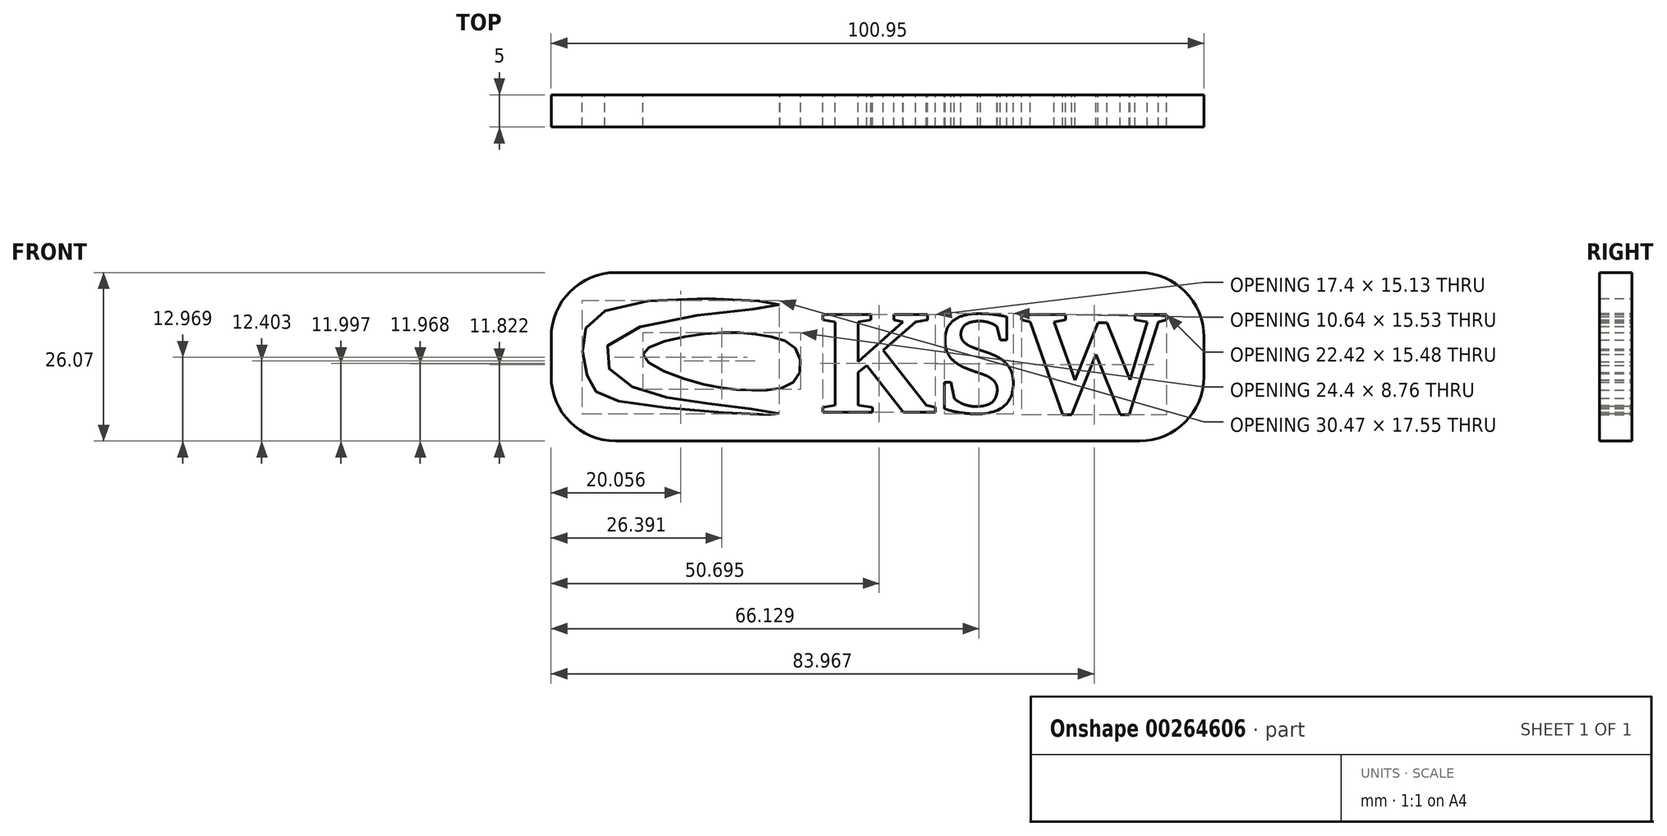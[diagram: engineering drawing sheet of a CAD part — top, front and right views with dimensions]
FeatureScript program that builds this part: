
annotation { "Feature Type Name" : "Feature", "Feature Type Description" : "" }
export const myFeature = defineFeature(function(context is Context, id is Id, definition is map)
    precondition{}
    {
        {
            var Q0;
            Q0=qCreatedBy(makeId("Front.planeOp"),FACE);
            var sketch = newSketch(context, id + "F0", { "sketchPlane" : qUnion([Q0])});
            skLineSegment(sketch, "E0.bottom", {"start": v(28.98, -26.09) * mm, "end": v(-51.97, -26.09) * mm});
            skLineSegment(sketch, "E0.top", {"start": v(28.98, -0.02) * mm, "end": v(-51.97, -0.02) * mm});
            skLineSegment(sketch, "E0.left", {"start": v(38.98, -16.09) * mm, "end": v(38.98, -10.02) * mm});
            skLineSegment(sketch, "E0.right", {"start": v(-61.97, -16.09) * mm, "end": v(-61.97, -10.02) * mm});
            skPoint(sketch, "E1.visualSharp", {"position": v(-61.97, -0.02) * mm});
            skArc(sketch, "E1.filletArc", {"start": v(-51.97, -0.02) * mm, "mid": v(-59.04, -2.95) * mm, "end": v(-61.97, -10.02) * mm});
            skPoint(sketch, "E2.visualSharp", {"position": v(-61.97, -26.09) * mm});
            skArc(sketch, "E2.filletArc", {"start": v(-61.97, -16.09) * mm, "mid": v(-59.04, -23.16) * mm, "end": v(-51.97, -26.09) * mm});
            skPoint(sketch, "E3.visualSharp", {"position": v(38.98, -26.09) * mm});
            skArc(sketch, "E3.filletArc", {"start": v(28.98, -26.09) * mm, "mid": v(36.05, -23.16) * mm, "end": v(38.98, -16.09) * mm});
            skPoint(sketch, "E4.visualSharp", {"position": v(38.98, -0.02) * mm});
            skArc(sketch, "E4.filletArc", {"start": v(38.98, -10.02) * mm, "mid": v(36.05, -2.95) * mm, "end": v(28.98, -0.02) * mm});
            skText(sketch, "E5", { "text": "KSW", "fontName": "Tinos-Bold.ttf"});
            skFitSpline(sketch, "E6", {"points": [v(-26.68, -5.02) * mm, v(-50.78, -5.02) * mm, v(-57.1, -10.47) * mm, v(-55.94, -17.07) * mm, v(-51.35, -19.94) * mm, v(-26.68, -21.95) * mm, v(-35.86, -20.51) * mm, v(-51.97, -16.09) * mm, v(-51.97, -10.02) * mm, v(-26.68, -5.02) * mm]});
            skFitSpline(sketch, "E7", {"points": [v(-47.78, -12.69) * mm, v(-39.9, -9.72) * mm, v(-29.83, -9.61) * mm, v(-24, -12.07) * mm, v(-24.22, -16.72) * mm, v(-30.4, -18.22) * mm, v(-39.59, -17) * mm, v(-47.78, -12.69) * mm]});
            const initialGuessF0  = {"E5": [-0.02037, -0.02166, 1, 0, 0.01664]};
            skSetInitialGuess(sketch, initialGuessF0);
            skSolve(sketch);
        }
        {
            var Q0;
            Q0=makeQuery(id+"F0.imprint","IMPRINT",FACE,{"disambiguationData":[TD([[makeQuery(id+"F0.imprint","IMPRINT",EDGE,{"derivedFrom":sQuery(id+"F0.wireOp",EDGE,"E0.bottom")}),-1.0]])]});
            extrude(context, id + "F1", {"entities" : qUnion([Q0]), "depth" : 5 * mm});
        }
    });
